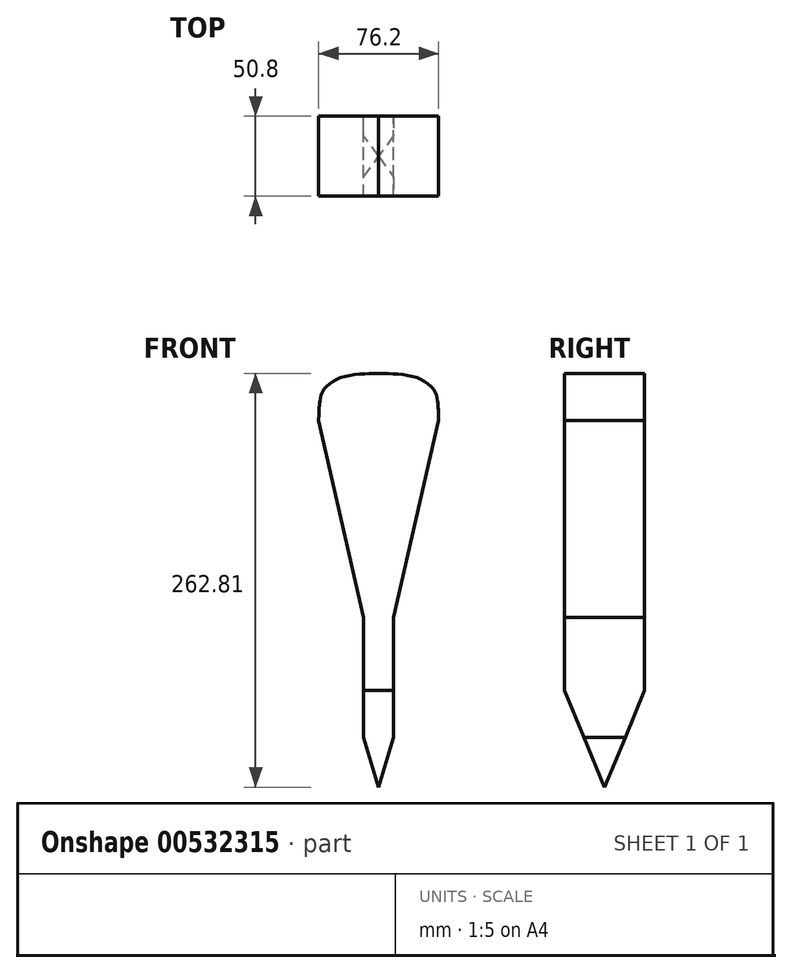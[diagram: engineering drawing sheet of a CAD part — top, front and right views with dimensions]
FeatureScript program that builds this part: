
annotation { "Feature Type Name" : "Feature", "Feature Type Description" : "" }
export const myFeature = defineFeature(function(context is Context, id is Id, definition is map)
    precondition{}
    {
        {
            var Q0;
            Q0=qCreatedBy(makeId("Front.planeOp"),FACE);
            var sketch = newSketch(context, id + "F0", { "sketchPlane" : qUnion([Q0])});
            skLineSegment(sketch, "E0", {"start": v(-9.52, 107.95) * mm, "end": v(-9.52, 31.75) * mm});
            skLineSegment(sketch, "E1", {"start": v(-9.52, 31.75) * mm, "end": v(0, 0) * mm});
            skLineSegment(sketch, "E2", {"start": v(0, 0) * mm, "end": v(9.53, 31.75) * mm});
            skLineSegment(sketch, "E3", {"start": v(9.53, 31.75) * mm, "end": v(9.53, 107.95) * mm});
            skLineSegment(sketch, "E4", {"start": v(9.52, 107.95) * mm, "end": v(38.1, 232.93) * mm});
            skLineSegment(sketch, "E5", {"start": v(-9.52, 107.95) * mm, "end": v(-38.1, 232.93) * mm});
            skLineSegment(sketch, "E6", {"start": v(-38.1, 232.93) * mm, "end": v(-9.53, 31.75) * mm, "construction": true});
            skLineSegment(sketch, "E7", {"start": v(9.52, 31.75) * mm, "end": v(38.1, 232.93) * mm, "construction": true});
            skLineSegment(sketch, "E8", {"start": v(0, 0) * mm, "end": v(0, 156.38) * mm, "construction": true});
            skFitSpline(sketch, "E9", {"points": [v(-38.1, 232.93) * mm, v(-37.6, 242.65) * mm, v(-36.83, 248.17) * mm, v(-31.75, 255.9) * mm, v(-17.94, 261.7) * mm, v(0, 262.81) * mm], "startDerivative": vector(0, 121.89) * mm, "endDerivative": vector(68.3, 2.28) * mm});
            skFitSpline(sketch, "E10.MirrorCS", {"points": [v(38.1, 232.93) * mm, v(37.6, 242.65) * mm, v(36.83, 248.17) * mm, v(31.75, 255.9) * mm, v(17.94, 261.7) * mm, v(0, 262.81) * mm], "startDerivative": vector(0, 121.89) * mm, "endDerivative": vector(-68.3, 2.28) * mm});
            skLineSegment(sketch, "E11", {"start": v(-38.1, 232.93) * mm, "end": v(38.1, 232.93) * mm, "construction": true});
            skSolve(sketch);
        }
        {
            var Q0;
            Q0=makeQuery(id+"F0.imprint","IMPRINT",FACE,{"disambiguationData":[TD([[makeQuery(id+"F0.imprint","IMPRINT",EDGE,{"derivedFrom":sQuery(id+"F0.wireOp",EDGE,"E0")}),1.0]])]});
            extrude(context, id + "F1", {"entities" : qUnion([Q0]), "depth" : 50.8 * mm, "offsetDistance" : 25.4 * mm, "symmetric" : true});
        }
        {
            var Q0;
            Q0=qCreatedBy(makeId("Right.planeOp"),FACE);
            var sketch = newSketch(context, id + "F2", { "sketchPlane" : qUnion([Q0])});
            skLineSegment(sketch, "E12", {"start": v(0, 0) * mm, "end": v(-29.16, 70.4) * mm});
            skLineSegment(sketch, "E13", {"start": v(-29.16, 70.4) * mm, "end": v(-87.5, 70.4) * mm});
            skLineSegment(sketch, "E14", {"start": v(-87.5, 70.4) * mm, "end": v(-87.5, -68.13) * mm});
            skLineSegment(sketch, "E15", {"start": v(-87.5, -68.13) * mm, "end": v(87.5, -68.13) * mm});
            skLineSegment(sketch, "E16", {"start": v(87.5, -68.13) * mm, "end": v(87.5, 70.4) * mm});
            skLineSegment(sketch, "E17", {"start": v(87.5, 70.4) * mm, "end": v(29.16, 70.4) * mm});
            skLineSegment(sketch, "E18", {"start": v(29.16, 70.4) * mm, "end": v(0, 0) * mm});
            skSolve(sketch);
        }
        {
            var Q0;
            Q0=makeQuery(id+"F2.imprint","IMPRINT",FACE,{"disambiguationData":[TD([[makeQuery(id+"F2.imprint","IMPRINT",EDGE,{"derivedFrom":sQuery(id+"F2.wireOp",EDGE,"E12")}),1.0]])]});
            extrude(context, id + "F3", {"entities" : qUnion([Q0]), "depth" : 50.8 * mm, "offsetDistance" : 25.4 * mm, "symmetric" : true});
        }
        {
            var Q0;
            Q0=makeQuery(id+"F3.opExtrude","SWEPT_BODY",BODY,{"disambiguationData":[OSD([sQuery(id+"F2.wireOp",EDGE,"E12"),sQuery(id+"F2.wireOp",EDGE,"E13"),sQuery(id+"F2.wireOp",EDGE,"E14"),sQuery(id+"F2.wireOp",EDGE,"E15"),sQuery(id+"F2.wireOp",EDGE,"E16"),sQuery(id+"F2.wireOp",EDGE,"E17"),sQuery(id+"F2.wireOp",EDGE,"E18")])]});
            var Q1;
            Q1=makeQuery(id+"F1.opExtrude","SWEPT_BODY",BODY,{"disambiguationData":[OSD([sQuery(id+"F0.wireOp",EDGE,"E0"),sQuery(id+"F0.wireOp",EDGE,"E1"),sQuery(id+"F0.wireOp",EDGE,"E2"),sQuery(id+"F0.wireOp",EDGE,"E3"),sQuery(id+"F0.wireOp",EDGE,"E4"),sQuery(id+"F0.wireOp",EDGE,"E5"),sQuery(id+"F0.wireOp",EDGE,"E9"),sQuery(id+"F0.wireOp",EDGE,"E10.MirrorCS")])]});
            booleanBodies(context, id + "F4", {"operationType" : BooleanOperationType.SUBTRACTION, "tools" : qUnion([Q0]), "targets" : qUnion([Q1])});
        }
    });
